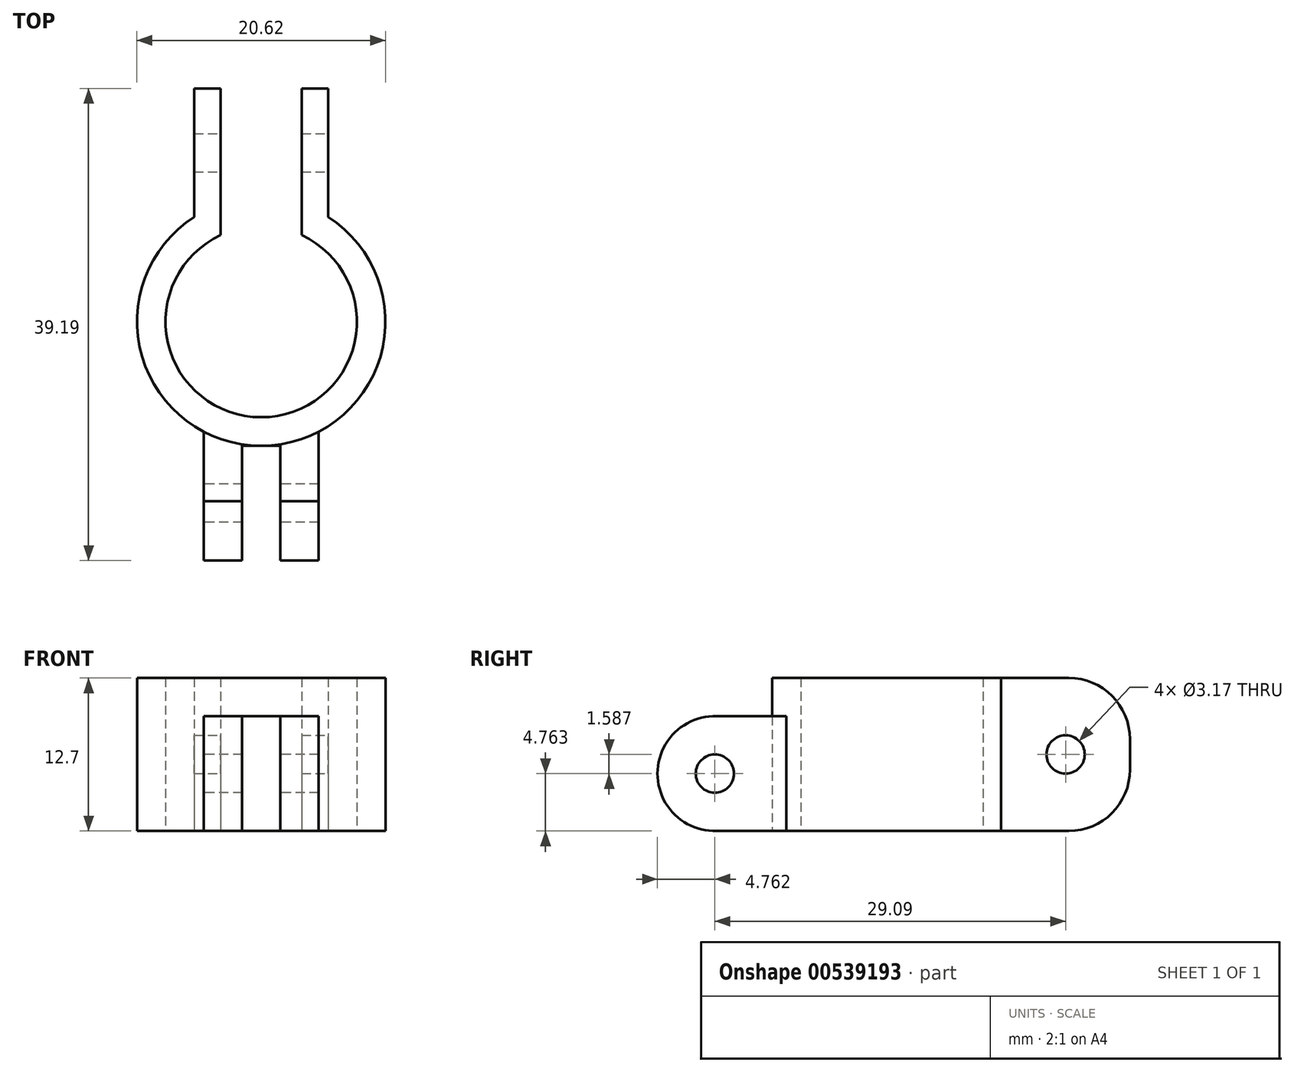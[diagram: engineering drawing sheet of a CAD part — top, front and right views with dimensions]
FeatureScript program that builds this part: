
annotation { "Feature Type Name" : "Feature", "Feature Type Description" : "" }
export const myFeature = defineFeature(function(context is Context, id is Id, definition is map)
    precondition{}
    {
        {
            var Q0;
            Q0=qCreatedBy(makeId("Top.planeOp"),FACE);
            var sketch = newSketch(context, id + "F0", { "sketchPlane" : qUnion([Q0])});
            skArc(sketch, "E0", {"start": v(-5.55, 8.68) * mm, "mid": v(0, -10.3) * mm, "end": v(5.55, 8.68) * mm});
            skLineSegment(sketch, "E1", {"start": v(0, 0) * mm, "end": v(0, 18.27) * mm});
            skLineSegment(sketch, "E2", {"start": v(-5.55, 8.68) * mm, "end": v(-5.55, 5.67) * mm});
            skLineSegment(sketch, "E3.MirrorCS", {"start": v(5.55, 8.68) * mm, "end": v(5.55, 5.67) * mm});
            skLineSegment(sketch, "E4.top", {"start": v(-5.55, 19.36) * mm, "end": v(-3.36, 19.36) * mm});
            skLineSegment(sketch, "E4.left", {"start": v(-5.55, 5.67) * mm, "end": v(-5.55, 19.36) * mm});
            skLineSegment(sketch, "E4.right", {"start": v(-3.36, 7.2) * mm, "end": v(-3.36, 19.36) * mm});
            skArc(sketch, "E5", {"start": v(-3.36, 7.2) * mm, "mid": v(-4.52, 6.52) * mm, "end": v(-5.55, 5.67) * mm});
            skCircle(sketch, "E6", {"center": v(0, 0) * mm, "radius": 7.94 * mm});
            skLineSegment(sketch, "E7.MirrorCS", {"start": v(5.55, 19.36) * mm, "end": v(3.36, 19.36) * mm});
            skLineSegment(sketch, "E8.MirrorCS", {"start": v(3.36, 7.2) * mm, "end": v(3.36, 19.36) * mm});
            skLineSegment(sketch, "E9.MirrorCS", {"start": v(5.55, 5.67) * mm, "end": v(5.55, 19.36) * mm});
            skSolve(sketch);
        }
        {
            var Q0;
            Q0=qCreatedBy(makeId("Right.planeOp"),FACE);
            var sketch = newSketch(context, id + "F1", { "sketchPlane" : qUnion([Q0])});
            skArc(sketch, "E10", {"start": v(-14.91, 9.52) * mm, "mid": v(-19.83, 4.76) * mm, "end": v(-14.91, 0) * mm});
            skCircle(sketch, "E11", {"center": v(-15.07, 4.76) * mm, "radius": 1.59 * mm});
            skLineSegment(sketch, "E12.bottom", {"start": v(-14.91, 9.52) * mm, "end": v(-7.94, 9.52) * mm});
            skLineSegment(sketch, "E12.top", {"start": v(-14.91, 0) * mm, "end": v(-7.94, 0) * mm});
            skLineSegment(sketch, "E12.right", {"start": v(-7.94, 9.52) * mm, "end": v(-7.94, 0) * mm});
            skLineSegment(sketch, "E13.trimOffspring", {"start": v(-14.91, 0) * mm, "end": v(-14.91, 0) * mm});
            skSolve(sketch);
        }
        {
            var Q0;
            {var subQ0=sQuery(id+"F0.wireOp",EDGE,"E0");Q0=makeQuery(id+"F0.imprint","IMPRINT",FACE,{"disambiguationData":[TD([[makeQuery(id+"F0.imprint","IMPRINT",EDGE,{"derivedFrom":subQ0}),1.0]])]});}
            var Q1;
            {var subQ3=sQuery(id+"F0.wireOp",EDGE,"E4.top");Q1=makeQuery(id+"F0.imprint","IMPRINT",FACE,{"disambiguationData":[TD([[makeQuery(id+"F0.imprint","IMPRINT",EDGE,{"derivedFrom":subQ3}),-1.0]])]});}
            var Q2;
            {var subQ4=sQuery(id+"F0.wireOp",EDGE,"E7.MirrorCS");Q2=makeQuery(id+"F0.imprint","IMPRINT",FACE,{"disambiguationData":[TD([[makeQuery(id+"F0.imprint","IMPRINT",EDGE,{"derivedFrom":subQ4}),1.0]])]});}
            extrude(context, id + "F2", {"entities" : qUnion([Q0, Q1, Q2]), "depth" : 12.7 * mm, "offsetDistance" : 25.4 * mm});
        }
        {
            var Q0;
            Q0=makeQuery(id+"F1.imprint","IMPRINT",FACE,{"disambiguationData":[TD([[makeQuery(id+"F1.imprint","IMPRINT",EDGE,{"derivedFrom":sQuery(id+"F1.wireOp",EDGE,"E10")}),1.0]])]});
            extrude(context, id + "F3", {"entities" : qUnion([Q0]), "operationType" : NewBodyOperationType.ADD, "endBound" : BoundingType.SYMMETRIC, "depth" : 9.52 * mm, "offsetDistance" : 25.4 * mm});
        }
        {
            var Q0;
            Q0=makeQuery(id+"F2.opExtrude","SWEPT_FACE",FACE,{"disambiguationData":[OSD([sQuery(id+"F0.wireOp",EDGE,"E9.MirrorCS")])]});
            var sketch = newSketch(context, id + "F4", { "sketchPlane" : qUnion([Q0])});
            skCircle(sketch, "E14", {"center": v(14.02, 6.35) * mm, "radius": 1.59 * mm});
            skSolve(sketch);
        }
        {
            var Q0;
            Q0=makeQuery(id+"F4.imprint","IMPRINT",FACE,{"disambiguationData":[TD([[makeQuery(id+"F4.imprint","IMPRINT",EDGE,{"derivedFrom":sQuery(id+"F4.wireOp",EDGE,"E14")}),1.0]])]});
            extrude(context, id + "F5", {"entities" : qUnion([Q0]), "operationType" : NewBodyOperationType.REMOVE, "endBound" : BoundingType.THROUGH_ALL, "oppositeDirection" : true, "depth" : 25.4 * mm, "offsetDistance" : 25.4 * mm});
        }
        {
            var Q0;
            Q0=makeQuery(id+"F2.opExtrude","SWEPT_BODY",BODY,{"disambiguationData":[OSD([sQuery(id+"F0.wireOp",EDGE,"E0"),sQuery(id+"F0.wireOp",EDGE,"E4.top"),sQuery(id+"F0.wireOp",EDGE,"E4.left"),sQuery(id+"F0.wireOp",EDGE,"E4.right"),sQuery(id+"F0.wireOp",EDGE,"E6"),sQuery(id+"F0.wireOp",EDGE,"E7.MirrorCS"),sQuery(id+"F0.wireOp",EDGE,"E8.MirrorCS"),sQuery(id+"F0.wireOp",EDGE,"E9.MirrorCS")])]});
            transform(context, id + "F6", {"entities" : qUnion([Q0]), "transformType" : TransformType.TRANSLATION_3D, "dx" : 0 * mm, "dy" : 0 * mm, "dz" : 0 * mm, "makeCopy" : true});
        }
        {
            var Q0;
            Q0=makeQuery(id+"F6.opPattern","COPY",BODY,{"derivedFrom":makeQuery(id+"F2.opExtrude","SWEPT_BODY",BODY,{"disambiguationData":[OSD([sQuery(id+"F0.wireOp",EDGE,"E0"),sQuery(id+"F0.wireOp",EDGE,"E4.top"),sQuery(id+"F0.wireOp",EDGE,"E4.left"),sQuery(id+"F0.wireOp",EDGE,"E4.right"),sQuery(id+"F0.wireOp",EDGE,"E6"),sQuery(id+"F0.wireOp",EDGE,"E7.MirrorCS"),sQuery(id+"F0.wireOp",EDGE,"E8.MirrorCS"),sQuery(id+"F0.wireOp",EDGE,"E9.MirrorCS")])]}),"instanceName":"1"});
            deleteBodies(context, id + "F7", {"entities" : qUnion([Q0])});
        }
        {
            var Q0;
            Q0=makeQuery(id+"F2.opExtrude","SWEPT_BODY",BODY,{"disambiguationData":[OSD([sQuery(id+"F0.wireOp",EDGE,"E0"),sQuery(id+"F0.wireOp",EDGE,"E4.top"),sQuery(id+"F0.wireOp",EDGE,"E4.left"),sQuery(id+"F0.wireOp",EDGE,"E4.right"),sQuery(id+"F0.wireOp",EDGE,"E6"),sQuery(id+"F0.wireOp",EDGE,"E7.MirrorCS"),sQuery(id+"F0.wireOp",EDGE,"E8.MirrorCS"),sQuery(id+"F0.wireOp",EDGE,"E9.MirrorCS")])]});
            transform(context, id + "F8", {"entities" : qUnion([Q0]), "transformType" : TransformType.TRANSLATION_3D, "dx" : 0 * mm, "dy" : 0 * mm, "dz" : 0 * mm, "makeCopy" : true});
        }
        {
            var Q0;
            Q0=qCreatedBy(makeId("Top.planeOp"),FACE);
            var sketch = newSketch(context, id + "F9", { "sketchPlane" : qUnion([Q0])});
            skLineSegment(sketch, "E15.bottom", {"start": v(0, -10.3) * mm, "end": v(1.59, -10.3) * mm});
            skLineSegment(sketch, "E15.top", {"start": v(0, -19.83) * mm, "end": v(1.59, -19.83) * mm});
            skLineSegment(sketch, "E15.left", {"start": v(0, -10.3) * mm, "end": v(0, -19.83) * mm});
            skLineSegment(sketch, "E15.right", {"start": v(1.59, -10.3) * mm, "end": v(1.59, -19.83) * mm});
            skLineSegment(sketch, "E16.MirrorCS", {"start": v(-1.59, -10.3) * mm, "end": v(-1.59, -19.83) * mm});
            skLineSegment(sketch, "E17.MirrorCS", {"start": v(0, -19.83) * mm, "end": v(-1.59, -19.83) * mm});
            skLineSegment(sketch, "E18.MirrorCS", {"start": v(0, -10.3) * mm, "end": v(-1.59, -10.3) * mm});
            skSolve(sketch);
        }
        {
            var Q0;
            Q0=makeQuery(id+"F9.imprint","IMPRINT",FACE,{"disambiguationData":[TD([[makeQuery(id+"F9.imprint","IMPRINT",EDGE,{"derivedFrom":sQuery(id+"F9.wireOp",EDGE,"E15.bottom")}),-1.0]])]});
            var Q1;
            Q1=makeQuery(id+"F9.imprint","IMPRINT",FACE,{"disambiguationData":[TD([[makeQuery(id+"F9.imprint","IMPRINT",EDGE,{"derivedFrom":sQuery(id+"F9.wireOp",EDGE,"E15.left")}),-1.0]])]});
            extrude(context, id + "F10", {"entities" : qUnion([Q0, Q1]), "operationType" : NewBodyOperationType.REMOVE, "depth" : 25.4 * mm, "offsetDistance" : 25.4 * mm});
        }
        {
            var Q0;
            Q0=makeQuery(id+"F2.opExtrude","SWEPT_BODY",BODY,{"disambiguationData":[OSD([sQuery(id+"F0.wireOp",EDGE,"E0"),sQuery(id+"F0.wireOp",EDGE,"E4.top"),sQuery(id+"F0.wireOp",EDGE,"E4.left"),sQuery(id+"F0.wireOp",EDGE,"E4.right"),sQuery(id+"F0.wireOp",EDGE,"E6"),sQuery(id+"F0.wireOp",EDGE,"E7.MirrorCS"),sQuery(id+"F0.wireOp",EDGE,"E8.MirrorCS"),sQuery(id+"F0.wireOp",EDGE,"E9.MirrorCS")])]});
            deleteBodies(context, id + "F11", {"entities" : qUnion([Q0])});
        }
        {
            var Q0;
            Q0=makeQuery(id+"F8.opPattern","COPY",EDGE,{"derivedFrom":makeQuery(id+"F2.opExtrude","CAP_EDGE",EDGE,{"disambiguationData":[OSD([sQuery(id+"F0.wireOp",EDGE,"E4.top")])],"isStart":false}),"instanceName":"1"});
            var Q1;
            Q1=makeQuery(id+"F8.opPattern","COPY",EDGE,{"derivedFrom":makeQuery(id+"F2.opExtrude","CAP_EDGE",EDGE,{"disambiguationData":[OSD([sQuery(id+"F0.wireOp",EDGE,"E7.MirrorCS")])],"isStart":false}),"instanceName":"1"});
            var Q2;
            Q2=makeQuery(id+"F8.opPattern","COPY",EDGE,{"derivedFrom":makeQuery(id+"F2.opExtrude","CAP_EDGE",EDGE,{"disambiguationData":[OSD([sQuery(id+"F0.wireOp",EDGE,"E4.top")])],"isStart":true}),"instanceName":"1"});
            var Q3;
            Q3=makeQuery(id+"F8.opPattern","COPY",EDGE,{"derivedFrom":makeQuery(id+"F2.opExtrude","CAP_EDGE",EDGE,{"disambiguationData":[OSD([sQuery(id+"F0.wireOp",EDGE,"E7.MirrorCS")])],"isStart":true}),"instanceName":"1"});
            fillet(context, id + "F12", {"entities" : qUnion([Q0, Q1, Q2, Q3]), "radius" : 5.08 * mm, "tangentPropagation" : true, "allowEdgeOverflow" : false});
        }
    });
